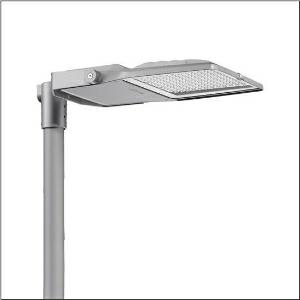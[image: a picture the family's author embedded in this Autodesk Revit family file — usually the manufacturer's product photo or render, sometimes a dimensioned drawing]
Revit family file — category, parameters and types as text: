
# Revit family: floodlight_fl_21_midi___pl33t_5xa7781e2f3a_b595
name_source: partatom
category: Lighting Fixtures
units: mm (PartAtom-declared; Revit-internal decimal feet)

## family parameters
Cut with Voids When Loaded = No
Host = Face
Light Source = No
Part Type = Normal
Room Calculation Point = No
Round Connector Dimension = Use Diameter
Shared = No

## types (1)
- --- (1 x LED, 26540 lm, 208.1 W, 3000K)
    Apparent Load = 208 VA
    CIE Flux Codes = 26 75 99 100 100
    Color Rendering = 70
    Color Temperature = 3000K
    Default Elevation = 1800 mm
    Description = Floodlight FL 21 midi, floodlight, primary light control with lens, of PMMA, primary optical cover: protective disc, of toughened safety glass, transparent, light distribution: PL33T, light emission: direct distribution, installation type: surface-mounted, LED, High Power LED, rated luminous flux: 26.540lm, luminous efficacy: 127lm/W, light colour: 730, colour temperature: 3000K, control gear: ECG iQ, control: optimised constant luminous flux control (CLO 2.0), Desk-Remote (wireless, voltage-free reading and setting of iQ features in the workshop via application-optimized NFC function/RFID function), Light-Fading, Smart-Wire, Night-Set, Lumen-Switch, Temp-Guard, Auto-Match, with terminal, 6-pole, mains connection: 220..240V, AC, 50/60Hz, start of lifetime: 208W, end of lifetime: 227W, reduction: 90W, luminaire housing, of diecast aluminium, powder-coated, Siteco® metallic grey (DB 702S), corrosivity category C5 according to DIN EN ISO 12944, mast bracket, of steel, galvanised, powder-coated, Siteco® metallic grey (DB 702S), protection rating (complete): IP66, insulation class (complete): insulation class I (protective earthing), certification: CE, protection symbol: D, impact resistance: IK08, permissible operating ambient temperature: -40..+40°C, permissible operating ambient temperature for outdoor applications: -40..+50°C, standard: DIN EN 12944, packaging unit: 1 piece

Light Distribution: PL33T
    Height = 76 mm
    Lamp = 1 x LED
    Lamp Light Flux = 26540 lm
    Lamp Power = 208.1 W
    Lamp count = 1
    Length = 657 mm
    Luminous efficacy = 128 lm/W
    Manufacturer = Siteco
    ModVariant = No
    Model = 5XA7781E2F3A
    Number of Poles = 1
    OnlyDefault = Yes
    Power Factor = 1
    Product Name = Floodlight FL 21 midi | PL33T
    Product group = floodlight | pylon top
    ProductGroupID = 6101
    Protection Class = Protection class I
    Protection Degree = IP 66
    RLX_Detail_Level = 1
    RlxData = <blob elided: 153469 chars, md5=0e76994a>
    Socket = socket
    Standby Power = 0 W
    System Light Flux = 26540 lm
    System Power = 208 W
    Type Comments = factory setting: luminous flux: 100 % | dim-lin: 254 | 710 mA
    Type Image = l_1007123.jpg
    URL = http://relux.com
    VarID = @adj_012625
    Voltage = 0 V
    Weight = 0.00 kg
    Width = 442 mm

## geometry (parser evidence)
native form markers: Blend x4, Sweep x11
no freeform markers — native parametric forms only
